# Revit family: CER
name_source: partatom
category: Lighting Fixtures
units: mm (PartAtom-declared; Revit-internal decimal feet)

## family parameters
Cut with Voids When Loaded = No
Host = Face
Light Source = Yes
OmniClass Number = 23.80.70.11.21
OmniClass Title = Emergency Lighting
Part Type = Normal
Room Calculation Point = No
Round Connector Dimension = Use Diameter
Shared = No

## types (1)
- CER
    Apparent Load = 0 VA
    Color Filter = 16777215
    Default Elevation = 48.000"
    Description = CE - LED Emergency Exit
    Dimming Lamp Color Temperature Shift = <None>
    Emit Shape Visible in Rendering = No
    Emit from Rectangle Length = 10.000"
    Emit from Rectangle Width = 5.000"
    Finish = White
    Glass = light Glass
    Lamp = LED Lamp
    Lens = Red Glass
    Load Classification = Lighting
    Manufacturer = Compass Products
    Model = CER
    Photometric Web File = generic
    Tilt Angle = 0.00°
    URL = https://www.currentlighting.com
    Voltage = 120 V
    Wattage Comments = 1.78 - 1.88 W

## geometry (parser evidence)
native form markers: Sweep x3
no freeform markers — native parametric forms only
